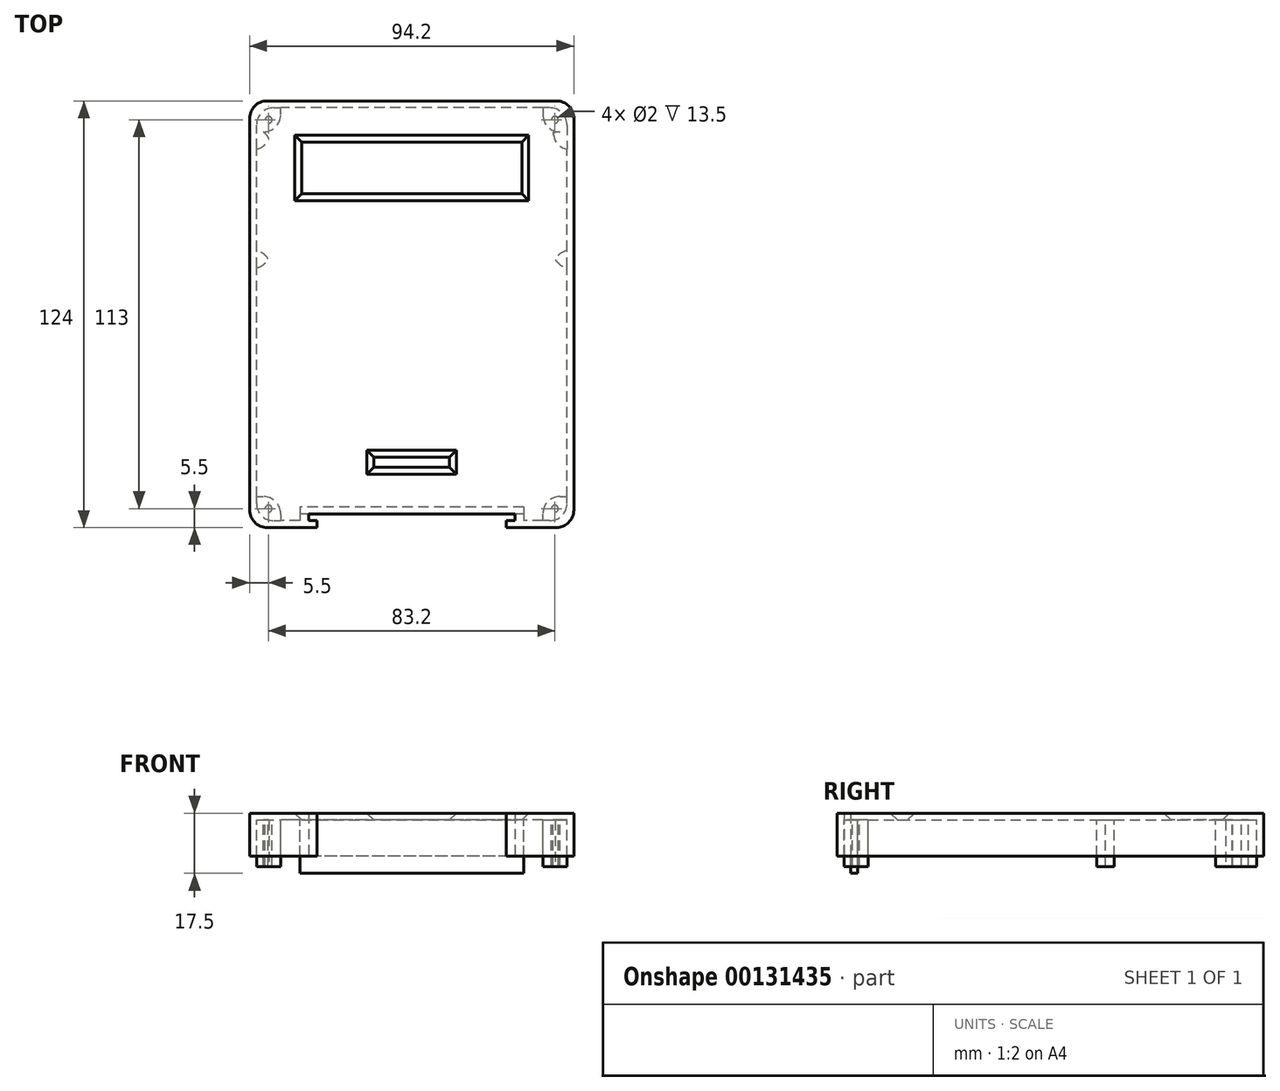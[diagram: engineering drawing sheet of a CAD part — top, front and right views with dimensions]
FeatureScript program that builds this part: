
annotation { "Feature Type Name" : "Feature", "Feature Type Description" : "" }
export const myFeature = defineFeature(function(context is Context, id is Id, definition is map)
    precondition{}
    {
        {
            var Q0;
            Q0=qCreatedBy(makeId("Top.planeOp"),FACE);
            var sketch = newSketch(context, id + "F0", { "sketchPlane" : qUnion([Q0])});
            skLineSegment(sketch, "E0.bottom", {"start": v(45.1, -62.5) * mm, "end": v(-45.1, -62.5) * mm});
            skLineSegment(sketch, "E0.top", {"start": v(45.1, 57.5) * mm, "end": v(-45.1, 57.5) * mm});
            skLineSegment(sketch, "E0.left", {"start": v(45.1, -62.5) * mm, "end": v(45.1, 57.5) * mm});
            skLineSegment(sketch, "E0.right", {"start": v(-45.1, -62.5) * mm, "end": v(-45.1, 57.5) * mm});
            skSolve(sketch);
        }
        {
            var Q0;
            Q0=makeQuery(id+"F0.imprint","IMPRINT",FACE,{"disambiguationData":[TD([[makeQuery(id+"F0.imprint","IMPRINT",EDGE,{"derivedFrom":sQuery(id+"F0.wireOp",EDGE,"E0.bottom")}),-1.0]])]});
            extrude(context, id + "F1", {"entities" : qUnion([Q0]), "depth" : 10.5 * mm});
        }
        {
            var Q0;
            Q0=makeQuery(id+"F1.opExtrude","CAP_FACE",FACE,{"disambiguationData":[OSD([sQuery(id+"F0.wireOp",EDGE,"E0.bottom"),sQuery(id+"F0.wireOp",EDGE,"E0.top"),sQuery(id+"F0.wireOp",EDGE,"E0.left"),sQuery(id+"F0.wireOp",EDGE,"E0.right")])],"isStart":true});
            shell(context, id + "F2", {"entities" : qUnion([Q0]), "thickness" : 2 * mm, "oppositeDirection" : true});
        }
        {
            var Q0;
            Q0=makeQuery(id+"F1.opExtrude","SWEPT_EDGE",EDGE,{"disambiguationData":[OSD([sQuery(id+"F0.wireOp",EDGE,"E0.bottom"),sQuery(id+"F0.wireOp",EDGE,"E0.right")])]});
            var Q1;
            Q1=makeQuery(id+"F1.opExtrude","SWEPT_EDGE",EDGE,{"disambiguationData":[OSD([sQuery(id+"F0.wireOp",EDGE,"E0.top"),sQuery(id+"F0.wireOp",EDGE,"E0.right")])]});
            var Q2;
            Q2=makeQuery(id+"F1.opExtrude","SWEPT_EDGE",EDGE,{"disambiguationData":[OSD([sQuery(id+"F0.wireOp",EDGE,"E0.bottom"),sQuery(id+"F0.wireOp",EDGE,"E0.left")])]});
            var Q3;
            Q3=makeQuery(id+"F1.opExtrude","SWEPT_EDGE",EDGE,{"disambiguationData":[OSD([sQuery(id+"F0.wireOp",EDGE,"E0.top"),sQuery(id+"F0.wireOp",EDGE,"E0.left")])]});
            var Q4;
            Q4=makeQuery(id+"F2.opShell","OFFSET_EDGE",EDGE,{"disambiguationData":[OSD([sQuery(id+"F0.wireOp",EDGE,"E0.top"),sQuery(id+"F0.wireOp",EDGE,"E0.right")])]});
            var Q5;
            Q5=makeQuery(id+"F2.opShell","OFFSET_EDGE",EDGE,{"disambiguationData":[OSD([sQuery(id+"F0.wireOp",EDGE,"E0.bottom"),sQuery(id+"F0.wireOp",EDGE,"E0.right")])]});
            var Q6;
            Q6=makeQuery(id+"F2.opShell","OFFSET_EDGE",EDGE,{"disambiguationData":[OSD([sQuery(id+"F0.wireOp",EDGE,"E0.top"),sQuery(id+"F0.wireOp",EDGE,"E0.left")])]});
            var Q7;
            Q7=makeQuery(id+"F2.opShell","OFFSET_EDGE",EDGE,{"disambiguationData":[OSD([sQuery(id+"F0.wireOp",EDGE,"E0.bottom"),sQuery(id+"F0.wireOp",EDGE,"E0.left")])]});
            fillet(context, id + "F3", {"entities" : qUnion([Q0, Q1, Q2, Q3, Q4, Q5, Q6, Q7]), "radius" : 5.08 * mm, "tangentPropagation" : true, "allowEdgeOverflow" : false});
        }
        {
            var Q0;
            Q0=makeQuery(id+"F2.opShell","OFFSET_FACE",FACE,{"disambiguationData":[OSD([sQuery(id+"F0.wireOp",EDGE,"E0.bottom"),sQuery(id+"F0.wireOp",EDGE,"E0.top"),sQuery(id+"F0.wireOp",EDGE,"E0.left"),sQuery(id+"F0.wireOp",EDGE,"E0.right")])]});
            var sketch = newSketch(context, id + "F4", { "sketchPlane" : qUnion([Q0])});
            skLineSegment(sketch, "E1.bottom", {"start": v(38.1, 62.5) * mm, "end": v(45.1, 62.5) * mm});
            skLineSegment(sketch, "E1.top", {"start": v(38.1, 55.5) * mm, "end": v(45.1, 55.5) * mm});
            skLineSegment(sketch, "E1.left", {"start": v(38.1, 62.5) * mm, "end": v(38.1, 55.5) * mm});
            skLineSegment(sketch, "E1.right", {"start": v(45.1, 62.5) * mm, "end": v(45.1, 55.5) * mm});
            skLineSegment(sketch, "E2.bottom", {"start": v(38.1, -57.5) * mm, "end": v(45.1, -57.5) * mm});
            skLineSegment(sketch, "E2.top", {"start": v(38.1, -50.5) * mm, "end": v(45.1, -50.5) * mm});
            skLineSegment(sketch, "E2.left", {"start": v(38.1, -57.5) * mm, "end": v(38.1, -50.5) * mm});
            skLineSegment(sketch, "E2.right", {"start": v(45.1, -57.5) * mm, "end": v(45.1, -50.5) * mm});
            skLineSegment(sketch, "E3.bottom", {"start": v(-45.1, -50.5) * mm, "end": v(-38.1, -50.5) * mm});
            skLineSegment(sketch, "E3.top", {"start": v(-45.1, -57.5) * mm, "end": v(-38.1, -57.5) * mm});
            skLineSegment(sketch, "E3.left", {"start": v(-45.1, -50.5) * mm, "end": v(-45.1, -57.5) * mm});
            skLineSegment(sketch, "E3.right", {"start": v(-38.1, -50.5) * mm, "end": v(-38.1, -57.5) * mm});
            skLineSegment(sketch, "E4.bottom", {"start": v(-45.1, 55.5) * mm, "end": v(-38.1, 55.5) * mm});
            skLineSegment(sketch, "E4.top", {"start": v(-45.1, 62.5) * mm, "end": v(-38.1, 62.5) * mm});
            skLineSegment(sketch, "E4.left", {"start": v(-45.1, 55.5) * mm, "end": v(-45.1, 62.5) * mm});
            skLineSegment(sketch, "E4.right", {"start": v(-38.1, 55.5) * mm, "end": v(-38.1, 62.5) * mm});
            skCircle(sketch, "E5", {"center": v(-41.6, 59) * mm, "radius": 1 * mm});
            skPoint(sketch, "E5.centerSnap0", {"position": v(-41.6, 55.5) * mm});
            skPoint(sketch, "E5.centerSnap1", {"position": v(-38.1, 59) * mm});
            skCircle(sketch, "E6", {"center": v(41.6, 59) * mm, "radius": 1 * mm});
            skPoint(sketch, "E6.centerSnap0", {"position": v(41.6, 55.5) * mm});
            skPoint(sketch, "E6.centerSnap1", {"position": v(38.1, 59) * mm});
            skCircle(sketch, "E7", {"center": v(41.6, -54) * mm, "radius": 1 * mm});
            skPoint(sketch, "E7.centerSnap0", {"position": v(38.1, -54) * mm});
            skPoint(sketch, "E7.centerSnap1", {"position": v(41.6, -50.5) * mm});
            skCircle(sketch, "E8", {"center": v(-41.6, -54) * mm, "radius": 1 * mm});
            skPoint(sketch, "E8.centerSnap0", {"position": v(-38.1, -54) * mm});
            skPoint(sketch, "E8.centerSnap1", {"position": v(-41.6, -50.5) * mm});
            skSolve(sketch);
        }
        {
            var Q0;
            Q0=qSketchRegion(id+"F4",true);
            extrude(context, id + "F5", {"entities" : qUnion([Q0]), "operationType" : NewBodyOperationType.ADD, "depth" : 13.5 * mm});
        }
        {
            var Q0;
            Q0=makeQuery(id+"F5.opExtrude","SWEPT_EDGE",EDGE,{"disambiguationData":[OSD([sQuery(id+"F4.wireOp",EDGE,"E1.top"),sQuery(id+"F4.wireOp",EDGE,"E1.left")])]});
            var Q1;
            Q1=makeQuery(id+"F5.opExtrude","SWEPT_EDGE",EDGE,{"disambiguationData":[OSD([sQuery(id+"F4.wireOp",EDGE,"E2.top"),sQuery(id+"F4.wireOp",EDGE,"E2.left")])]});
            var Q2;
            Q2=makeQuery(id+"F5.opExtrude","SWEPT_EDGE",EDGE,{"disambiguationData":[OSD([sQuery(id+"F4.wireOp",EDGE,"E3.bottom"),sQuery(id+"F4.wireOp",EDGE,"E3.right")])]});
            var Q3;
            Q3=makeQuery(id+"F5.opExtrude","SWEPT_EDGE",EDGE,{"disambiguationData":[OSD([sQuery(id+"F4.wireOp",EDGE,"E4.bottom"),sQuery(id+"F4.wireOp",EDGE,"E4.right")])]});
            fillet(context, id + "F6", {"entities" : qUnion([Q0, Q1, Q2, Q3]), "radius" : 5 * mm, "tangentPropagation" : true, "allowEdgeOverflow" : false});
        }
        {
            var Q0;
            {var subQ0=sQuery(id+"F0.wireOp",EDGE,"E0.bottom");var subQ1=sQuery(id+"F0.wireOp",EDGE,"E0.top");var subQ2=sQuery(id+"F0.wireOp",EDGE,"E0.left");var subQ3=sQuery(id+"F0.wireOp",EDGE,"E0.right");Q0=makeQuery(id+"F5.boolean.opBoolean","SPLIT",FACE,{"disambiguationData":[TD([makeQuery(id+"F2.opShell","OFFSET_FACE",FACE,{"disambiguationData":[OSD([subQ0])]})])],"derivedFrom":makeQuery(id+"F2.opShell","OFFSET_FACE",FACE,{"disambiguationData":[OSD([subQ0,subQ1,subQ2,subQ3])]})});}
            var sketch = newSketch(context, id + "F7", { "sketchPlane" : qUnion([Q0])});
            skLineSegment(sketch, "E9.bottom", {"start": v(32, -47.5) * mm, "end": v(-32, -47.5) * mm});
            skLineSegment(sketch, "E9.top", {"start": v(32, -32.5) * mm, "end": v(-32, -32.5) * mm});
            skLineSegment(sketch, "E9.left", {"start": v(32, -47.5) * mm, "end": v(32, -32.5) * mm});
            skLineSegment(sketch, "E9.right", {"start": v(-32, -47.5) * mm, "end": v(-32, -32.5) * mm});
            skLineSegment(sketch, "E10", {"start": v(0, -47.5) * mm, "end": v(0, -57.5) * mm});
            skSolve(sketch);
        }
        {
            var Q0;
            Q0 = qSketchRegion(id + "F7", true);
            extrude(context, id + "F8", {"entities" : qUnion([Q0]), "operationType" : NewBodyOperationType.REMOVE, "endBound" : BoundingType.THROUGH_ALL, "oppositeDirection" : true, "depth" : 25 * mm, "hasDraft" : true, "draftAngle" : 45 * degree});
        }
        {
            var Q0;
            {var subQ0=sQuery(id+"F0.wireOp",EDGE,"E0.left");var subQ1=sQuery(id+"F0.wireOp",EDGE,"E0.bottom");var subQ2=sQuery(id+"F0.wireOp",EDGE,"E0.top");var subQ3=sQuery(id+"F0.wireOp",EDGE,"E0.right");Q0=makeQuery(id+"F5.boolean.opBoolean","SPLIT",FACE,{"disambiguationData":[TD([makeQuery(id+"F2.opShell","OFFSET_FACE",FACE,{"disambiguationData":[OSD([subQ1])]})])],"derivedFrom":makeQuery(id+"F2.opShell","OFFSET_FACE",FACE,{"disambiguationData":[OSD([subQ1,subQ2,subQ0,subQ3])]})});}
            var sketch = newSketch(context, id + "F9", { "sketchPlane" : qUnion([Q0])});
            skLineSegment(sketch, "E11.bottom", {"start": v(35, -22.5) * mm, "end": v(-35, -22.5) * mm});
            skLineSegment(sketch, "E11.top", {"start": v(35, 55.5) * mm, "end": v(-35, 55.5) * mm});
            skLineSegment(sketch, "E11.left", {"start": v(35, -22.5) * mm, "end": v(35, 55.5) * mm});
            skLineSegment(sketch, "E11.right", {"start": v(-35, -22.5) * mm, "end": v(-35, 55.5) * mm});
            skLineSegment(sketch, "E12", {"start": v(0, 55.5) * mm, "end": v(0, 62.5) * mm});
            skLineSegment(sketch, "E13.bottom", {"start": v(11, 44) * mm, "end": v(-11, 44) * mm});
            skLineSegment(sketch, "E13.top", {"start": v(11, 47) * mm, "end": v(-11, 47) * mm});
            skLineSegment(sketch, "E13.left", {"start": v(11, 44) * mm, "end": v(11, 47) * mm});
            skLineSegment(sketch, "E13.right", {"start": v(-11, 44) * mm, "end": v(-11, 47) * mm});
            skLineSegment(sketch, "E14", {"start": v(0, 47) * mm, "end": v(0, 55.5) * mm});
            skLineSegment(sketch, "E15", {"start": v(0, -32.5) * mm, "end": v(0, -22.5) * mm});
            skSolve(sketch);
        }
        {
            var Q0;
            {var subQ5=makeQuery(id+"F8.boolean.opBoolean","COPY",EDGE,{"derivedFrom":makeQuery(id+"F8.opExtrude","CAP_EDGE",EDGE,{"disambiguationData":[OSD([sQuery(id+"F7.wireOp",EDGE,"E9.top")])],"isStart":true})});Q0=makeQuery(id+"F9.imprint","IMPRINT",FACE,{"disambiguationData":[TD([[makeQuery(id+"F9.imprint","IMPRINT",EDGE,{"derivedFrom":subQ5}),1.0]])]});}
            var Q1;
            Q1=makeQuery(id+"F9.imprint","IMPRINT",FACE,{"disambiguationData":[TD([[makeQuery(id+"F9.imprint","IMPRINT",EDGE,{"derivedFrom":sQuery(id+"F9.wireOp",EDGE,"E13.bottom")}),-1.0]])]});
            extrude(context, id + "F10", {"entities" : qUnion([Q0, Q1]), "operationType" : NewBodyOperationType.REMOVE, "oppositeDirection" : true, "depth" : 25 * mm, "hasDraft" : true, "draftAngle" : 45 * degree});
        }
        {
            var Q0;
            Q0=makeQuery(id+"F5.opExtrude","SWEPT_EDGE",EDGE,{"disambiguationData":[OSD([sQuery(id+"F4.wireOp",EDGE,"E2.bottom"),sQuery(id+"F4.wireOp",EDGE,"E2.right")])]});
            var Q1;
            Q1=makeQuery(id+"F5.opExtrude","SWEPT_EDGE",EDGE,{"disambiguationData":[OSD([sQuery(id+"F4.wireOp",EDGE,"E3.top"),sQuery(id+"F4.wireOp",EDGE,"E3.left")])]});
            var Q2;
            Q2=makeQuery(id+"F5.opExtrude","SWEPT_EDGE",EDGE,{"disambiguationData":[OSD([sQuery(id+"F4.wireOp",EDGE,"E4.top"),sQuery(id+"F4.wireOp",EDGE,"E4.left")])]});
            var Q3;
            Q3=makeQuery(id+"F5.opExtrude","SWEPT_EDGE",EDGE,{"disambiguationData":[OSD([sQuery(id+"F4.wireOp",EDGE,"E1.bottom"),sQuery(id+"F4.wireOp",EDGE,"E1.right")])]});
            fillet(context, id + "F11", {"entities" : qUnion([Q0, Q1, Q2, Q3]), "radius" : 5 * mm, "tangentPropagation" : true, "allowEdgeOverflow" : false});
        }
        {
            var Q0;
            Q0=makeQuery(id+"F2.opShell","OFFSET_FACE",FACE,{"disambiguationData":[OSD([sQuery(id+"F0.wireOp",EDGE,"E0.bottom")])]});
            var sketch = newSketch(context, id + "F12", { "sketchPlane" : qUnion([Q0])});
            skLineSegment(sketch, "E16.bottom", {"start": v(32.5, 0) * mm, "end": v(-32.5, 0) * mm});
            skLineSegment(sketch, "E16.top", {"start": v(32.5, 10.5) * mm, "end": v(-32.5, 10.5) * mm});
            skLineSegment(sketch, "E16.left", {"start": v(32.5, 0) * mm, "end": v(32.5, 10.5) * mm});
            skLineSegment(sketch, "E16.right", {"start": v(-32.5, 0) * mm, "end": v(-32.5, 10.5) * mm});
            skLineSegment(sketch, "E17", {"start": v(0, 10.5) * mm, "end": v(0, 10.5) * mm});
            skSolve(sketch);
        }
        {
            var Q0;
            Q0 = qSketchRegion(id + "F12", true);
            var Q1;
            Q1=makeQuery(id+"F12.imprint","IMPRINT",FACE,{"disambiguationData":[TD([[makeQuery(id+"F12.imprint","IMPRINT",EDGE,{"derivedFrom":sQuery(id+"F12.wireOp",EDGE,"E16.bottom")}),1.0]])]});
            extrude(context, id + "F13", {"entities" : qUnion([Q0, Q1]), "operationType" : NewBodyOperationType.ADD, "depth" : 4 * mm});
        }
        {
            var Q0;
            Q0=makeQuery(id+"F13.boolean.opBoolean","MERGE",FACE,{"derivedFrom":[makeQuery(id+"F1.opExtrude","CAP_FACE",FACE,{"disambiguationData":[OSD([sQuery(id+"F0.wireOp",EDGE,"E0.bottom"),sQuery(id+"F0.wireOp",EDGE,"E0.top"),sQuery(id+"F0.wireOp",EDGE,"E0.left"),sQuery(id+"F0.wireOp",EDGE,"E0.right")])],"isStart":true}),makeQuery(id+"F13.opExtrude","SWEPT_FACE",FACE,{"disambiguationData":[OSD([sQuery(id+"F12.wireOp",EDGE,"E16.bottom")])]})]});
            var sketch = newSketch(context, id + "F14", { "sketchPlane" : qUnion([Q0])});
            skLineSegment(sketch, "E18.bottom", {"start": v(-27.5, 64.5) * mm, "end": v(27.5, 64.5) * mm});
            skLineSegment(sketch, "E18.top", {"start": v(-27.5, 60.5) * mm, "end": v(27.5, 60.5) * mm});
            skLineSegment(sketch, "E18.left", {"start": v(-27.5, 64.5) * mm, "end": v(-27.5, 60.5) * mm});
            skLineSegment(sketch, "E18.right", {"start": v(27.5, 64.5) * mm, "end": v(27.5, 60.5) * mm});
            skLineSegment(sketch, "E19", {"start": v(0, 60.5) * mm, "end": v(0, 58.5) * mm});
            skLineSegment(sketch, "E20.bottom", {"start": v(27.5, 60.5) * mm, "end": v(30, 60.5) * mm});
            skLineSegment(sketch, "E20.top", {"start": v(27.5, 62.5) * mm, "end": v(30, 62.5) * mm});
            skLineSegment(sketch, "E20.left", {"start": v(27.5, 60.5) * mm, "end": v(27.5, 62.5) * mm});
            skLineSegment(sketch, "E20.right", {"start": v(30, 60.5) * mm, "end": v(30, 62.5) * mm});
            skLineSegment(sketch, "E21.bottom", {"start": v(-27.5, 60.5) * mm, "end": v(-30, 60.5) * mm});
            skLineSegment(sketch, "E21.top", {"start": v(-27.5, 62.5) * mm, "end": v(-30, 62.5) * mm});
            skLineSegment(sketch, "E21.left", {"start": v(-27.5, 60.5) * mm, "end": v(-27.5, 62.5) * mm});
            skLineSegment(sketch, "E21.right", {"start": v(-30, 60.5) * mm, "end": v(-30, 62.5) * mm});
            skLineSegment(sketch, "E22", {"start": v(28.75, 60.5) * mm, "end": v(28.75, 58.5) * mm});
            skLineSegment(sketch, "E23", {"start": v(-28.75, 60.5) * mm, "end": v(-28.75, 58.5) * mm});
            skSolve(sketch);
        }
        {
            var Q0;
            Q0 = qSketchRegion(id + "F14", true);
            var Q1;
            Q1=makeQuery(id+"F14.imprint","IMPRINT",FACE,{"disambiguationData":[TD([[makeQuery(id+"F14.imprint","IMPRINT",EDGE,{"derivedFrom":sQuery(id+"F14.wireOp",EDGE,"E20.top")}),-1.0]])]});
            extrude(context, id + "F15", {"entities" : qUnion([Q0, Q1]), "operationType" : NewBodyOperationType.REMOVE, "oppositeDirection" : true, "depth" : 25 * mm});
        }
        {
            var Q0;
            Q0=makeQuery(id+"F13.boolean.opBoolean","MERGE",FACE,{"derivedFrom":[makeQuery(id+"F1.opExtrude","CAP_FACE",FACE,{"disambiguationData":[OSD([sQuery(id+"F0.wireOp",EDGE,"E0.bottom"),sQuery(id+"F0.wireOp",EDGE,"E0.top"),sQuery(id+"F0.wireOp",EDGE,"E0.left"),sQuery(id+"F0.wireOp",EDGE,"E0.right")])],"isStart":true}),makeQuery(id+"F13.opExtrude","SWEPT_FACE",FACE,{"disambiguationData":[OSD([sQuery(id+"F12.wireOp",EDGE,"E16.bottom")])]})]});
            var sketch = newSketch(context, id + "F16", { "sketchPlane" : qUnion([Q0])});
            skLineSegment(sketch, "E24.bottom", {"start": v(32.5, 58.5) * mm, "end": v(-32.5, 58.5) * mm});
            skLineSegment(sketch, "E24.top", {"start": v(32.5, 60.5) * mm, "end": v(-32.5, 60.5) * mm});
            skLineSegment(sketch, "E24.left", {"start": v(32.5, 58.5) * mm, "end": v(32.5, 60.5) * mm});
            skLineSegment(sketch, "E24.right", {"start": v(-32.5, 58.5) * mm, "end": v(-32.5, 60.5) * mm});
            skSolve(sketch);
        }
        {
            var Q0;
            Q0 = qSketchRegion(id + "F16", true);
            var Q1;
            Q1=makeQuery(id+"F16.imprint","IMPRINT",FACE,{"disambiguationData":[TD([[makeQuery(id+"F16.imprint","IMPRINT",EDGE,{"derivedFrom":sQuery(id+"F16.wireOp",EDGE,"E24.bottom")}),-1.0]])]});
            extrude(context, id + "F17", {"entities" : qUnion([Q0, Q1]), "operationType" : NewBodyOperationType.ADD, "depth" : 5 * mm});
        }
        {
            var Q0;
            {var subQ0=sQuery(id+"F0.wireOp",EDGE,"E0.top");var subQ1=sQuery(id+"F0.wireOp",EDGE,"E0.bottom");var subQ2=sQuery(id+"F0.wireOp",EDGE,"E0.left");var subQ3=sQuery(id+"F0.wireOp",EDGE,"E0.right");Q0=makeQuery(id+"F5.boolean.opBoolean","SPLIT",FACE,{"disambiguationData":[TD([makeQuery(id+"F2.opShell","OFFSET_FACE",FACE,{"disambiguationData":[OSD([subQ1])]})])],"derivedFrom":makeQuery(id+"F2.opShell","OFFSET_FACE",FACE,{"disambiguationData":[OSD([subQ1,subQ0,subQ2,subQ3])]})});}
            var sketch = newSketch(context, id + "F18", { "sketchPlane" : qUnion([Q0])});
            skLineSegment(sketch, "E25.bottom", {"start": v(45.1, -50.5) * mm, "end": v(41.1, -50.5) * mm});
            skLineSegment(sketch, "E25.top", {"start": v(45.1, 28.5) * mm, "end": v(41.1, 28.5) * mm});
            skLineSegment(sketch, "E25.left", {"start": v(45.1, -50.5) * mm, "end": v(45.1, 28.5) * mm});
            skLineSegment(sketch, "E25.right", {"start": v(41.1, -50.5) * mm, "end": v(41.1, 28.5) * mm});
            skLineSegment(sketch, "E26.bottom", {"start": v(-45.1, -50.5) * mm, "end": v(-41.1, -50.5) * mm});
            skLineSegment(sketch, "E26.top", {"start": v(-45.1, 28.5) * mm, "end": v(-41.1, 28.5) * mm});
            skLineSegment(sketch, "E26.left", {"start": v(-45.1, -50.5) * mm, "end": v(-45.1, 28.5) * mm});
            skLineSegment(sketch, "E26.right", {"start": v(-41.1, -50.5) * mm, "end": v(-41.1, 28.5) * mm});
            skLineSegment(sketch, "E27.bottom", {"start": v(41.1, 28.5) * mm, "end": v(45.1, 28.5) * mm});
            skLineSegment(sketch, "E27.top", {"start": v(41.1, 23.5) * mm, "end": v(45.1, 23.5) * mm});
            skLineSegment(sketch, "E27.left", {"start": v(41.1, 28.5) * mm, "end": v(41.1, 23.5) * mm});
            skLineSegment(sketch, "E27.right", {"start": v(45.1, 28.5) * mm, "end": v(45.1, 23.5) * mm});
            skLineSegment(sketch, "E28.bottom", {"start": v(41.1, -50.5) * mm, "end": v(45.1, -50.5) * mm});
            skLineSegment(sketch, "E28.top", {"start": v(41.1, -45.5) * mm, "end": v(45.1, -45.5) * mm});
            skLineSegment(sketch, "E28.left", {"start": v(41.1, -50.5) * mm, "end": v(41.1, -45.5) * mm});
            skLineSegment(sketch, "E28.right", {"start": v(45.1, -50.5) * mm, "end": v(45.1, -45.5) * mm});
            skLineSegment(sketch, "E29.bottom", {"start": v(-41.1, -50.5) * mm, "end": v(-45.1, -50.5) * mm});
            skLineSegment(sketch, "E29.top", {"start": v(-41.1, -45.5) * mm, "end": v(-45.1, -45.5) * mm});
            skLineSegment(sketch, "E29.left", {"start": v(-41.1, -50.5) * mm, "end": v(-41.1, -45.5) * mm});
            skLineSegment(sketch, "E29.right", {"start": v(-45.1, -50.5) * mm, "end": v(-45.1, -45.5) * mm});
            skLineSegment(sketch, "E30.bottom", {"start": v(-41.1, 28.5) * mm, "end": v(-45.1, 28.5) * mm});
            skLineSegment(sketch, "E30.top", {"start": v(-41.1, 23.5) * mm, "end": v(-45.1, 23.5) * mm});
            skLineSegment(sketch, "E30.left", {"start": v(-41.1, 28.5) * mm, "end": v(-41.1, 23.5) * mm});
            skLineSegment(sketch, "E30.right", {"start": v(-45.1, 28.5) * mm, "end": v(-45.1, 23.5) * mm});
            skLineSegment(sketch, "E31.bottom", {"start": v(-41.1, -11) * mm, "end": v(-45.1, -11) * mm});
            skLineSegment(sketch, "E31.top", {"start": v(-41.1, -16) * mm, "end": v(-45.1, -16) * mm});
            skLineSegment(sketch, "E31.left", {"start": v(-41.1, -11) * mm, "end": v(-41.1, -16) * mm});
            skLineSegment(sketch, "E31.right", {"start": v(-45.1, -11) * mm, "end": v(-45.1, -16) * mm});
            skLineSegment(sketch, "E32.bottom", {"start": v(41.1, -11) * mm, "end": v(45.1, -11) * mm});
            skLineSegment(sketch, "E32.top", {"start": v(41.1, -16) * mm, "end": v(45.1, -16) * mm});
            skLineSegment(sketch, "E32.left", {"start": v(41.1, -11) * mm, "end": v(41.1, -16) * mm});
            skLineSegment(sketch, "E32.right", {"start": v(45.1, -11) * mm, "end": v(45.1, -16) * mm});
            skLineSegment(sketch, "E33.left", {"start": v(41.1, -45.5) * mm, "end": v(41.1, -50.5) * mm});
            skLineSegment(sketch, "E33.right", {"start": v(45.1, -45.5) * mm, "end": v(45.1, -50.5) * mm});
            skSolve(sketch);
        }
        {
            var Q0;
            Q0=makeQuery(id+"F18.imprint","IMPRINT",FACE,{"disambiguationData":[TD([[makeQuery(id+"F18.imprint","IMPRINT",EDGE,{"derivedFrom":sQuery(id+"F18.wireOp",EDGE,"E27.bottom")}),-1.0]])]});
            var Q1;
            Q1=makeQuery(id+"F18.imprint","IMPRINT",FACE,{"disambiguationData":[TD([[makeQuery(id+"F18.imprint","IMPRINT",EDGE,{"derivedFrom":sQuery(id+"F18.wireOp",EDGE,"E29.top")}),1.0]])]});
            var Q2;
            Q2=makeQuery(id+"F18.imprint","IMPRINT",FACE,{"disambiguationData":[TD([[makeQuery(id+"F18.imprint","IMPRINT",EDGE,{"derivedFrom":sQuery(id+"F18.wireOp",EDGE,"E30.bottom")}),1.0]])]});
            var Q3;
            Q3=makeQuery(id+"F18.imprint","IMPRINT",FACE,{"disambiguationData":[TD([[makeQuery(id+"F18.imprint","IMPRINT",EDGE,{"derivedFrom":sQuery(id+"F18.wireOp",EDGE,"E31.bottom")}),1.0]])]});
            var Q4;
            Q4=makeQuery(id+"F18.imprint","IMPRINT",FACE,{"disambiguationData":[TD([[makeQuery(id+"F18.imprint","IMPRINT",EDGE,{"derivedFrom":sQuery(id+"F18.wireOp",EDGE,"E32.bottom")}),-1.0]])]});
            var Q5;
            Q5=makeQuery(id+"F18.imprint","IMPRINT",FACE,{"disambiguationData":[TD([[makeQuery(id+"F18.imprint","IMPRINT",EDGE,{"derivedFrom":sQuery(id+"F18.wireOp",EDGE,"E28.top")}),-1.0]])]});
            extrude(context, id + "F19", {"entities" : qUnion([Q0, Q1, Q2, Q3, Q4, Q5]), "operationType" : NewBodyOperationType.ADD, "depth" : 13.5 * mm});
        }
        {
            var Q0;
            Q0=makeQuery(id+"F19.opExtrude","SWEPT_EDGE",EDGE,{"disambiguationData":[OSD([sQuery(id+"F18.wireOp",EDGE,"E28.bottom"),sQuery(id+"F18.wireOp",EDGE,"E33.left")])]});
            var Q1;
            Q1=makeQuery(id+"F19.opExtrude","SWEPT_EDGE",EDGE,{"disambiguationData":[OSD([sQuery(id+"F18.wireOp",EDGE,"E25.right"),sQuery(id+"F18.wireOp",EDGE,"E28.top"),sQuery(id+"F18.wireOp",EDGE,"E33.left")])]});
            fillet(context, id + "F20", {"entities" : qUnion([Q0, Q1]), "radius" : 5 * mm, "tangentPropagation" : true, "allowEdgeOverflow" : false});
        }
        {
            var Q0;
            Q0=makeQuery(id+"F19.opExtrude","SWEPT_EDGE",EDGE,{"disambiguationData":[OSD([sQuery(id+"F18.wireOp",EDGE,"E27.bottom"),sQuery(id+"F18.wireOp",EDGE,"E27.left")])]});
            var Q1;
            Q1=makeQuery(id+"F19.opExtrude","SWEPT_EDGE",EDGE,{"disambiguationData":[OSD([sQuery(id+"F18.wireOp",EDGE,"E25.right"),sQuery(id+"F18.wireOp",EDGE,"E27.top"),sQuery(id+"F18.wireOp",EDGE,"E27.left")])]});
            var Q2;
            Q2=makeQuery(id+"F19.opExtrude","SWEPT_EDGE",EDGE,{"disambiguationData":[OSD([sQuery(id+"F18.wireOp",EDGE,"E25.right"),sQuery(id+"F18.wireOp",EDGE,"E32.bottom"),sQuery(id+"F18.wireOp",EDGE,"E32.left")])]});
            var Q3;
            Q3=makeQuery(id+"F19.opExtrude","SWEPT_EDGE",EDGE,{"disambiguationData":[OSD([sQuery(id+"F18.wireOp",EDGE,"E25.right"),sQuery(id+"F18.wireOp",EDGE,"E32.top"),sQuery(id+"F18.wireOp",EDGE,"E32.left")])]});
            var Q4;
            Q4=makeQuery(id+"F19.opExtrude","SWEPT_EDGE",EDGE,{"disambiguationData":[OSD([sQuery(id+"F18.wireOp",EDGE,"E29.bottom"),sQuery(id+"F18.wireOp",EDGE,"E29.left")])]});
            var Q5;
            Q5=makeQuery(id+"F19.opExtrude","SWEPT_EDGE",EDGE,{"disambiguationData":[OSD([sQuery(id+"F18.wireOp",EDGE,"E26.right"),sQuery(id+"F18.wireOp",EDGE,"E29.top"),sQuery(id+"F18.wireOp",EDGE,"E29.left")])]});
            var Q6;
            Q6=makeQuery(id+"F19.opExtrude","SWEPT_EDGE",EDGE,{"disambiguationData":[OSD([sQuery(id+"F18.wireOp",EDGE,"E26.right"),sQuery(id+"F18.wireOp",EDGE,"E31.top"),sQuery(id+"F18.wireOp",EDGE,"E31.left")])]});
            var Q7;
            Q7=makeQuery(id+"F19.opExtrude","SWEPT_EDGE",EDGE,{"disambiguationData":[OSD([sQuery(id+"F18.wireOp",EDGE,"E26.right"),sQuery(id+"F18.wireOp",EDGE,"E31.bottom"),sQuery(id+"F18.wireOp",EDGE,"E31.left")])]});
            var Q8;
            Q8=makeQuery(id+"F19.opExtrude","SWEPT_EDGE",EDGE,{"disambiguationData":[OSD([sQuery(id+"F18.wireOp",EDGE,"E26.right"),sQuery(id+"F18.wireOp",EDGE,"E30.top"),sQuery(id+"F18.wireOp",EDGE,"E30.left")])]});
            var Q9;
            Q9=makeQuery(id+"F19.opExtrude","SWEPT_EDGE",EDGE,{"disambiguationData":[OSD([sQuery(id+"F18.wireOp",EDGE,"E30.bottom"),sQuery(id+"F18.wireOp",EDGE,"E30.left")])]});
            fillet(context, id + "F21", {"entities" : qUnion([Q0, Q1, Q2, Q3, Q4, Q5, Q6, Q7, Q8, Q9]), "radius" : 5 * mm, "tangentPropagation" : true, "allowEdgeOverflow" : false});
        }
    });
